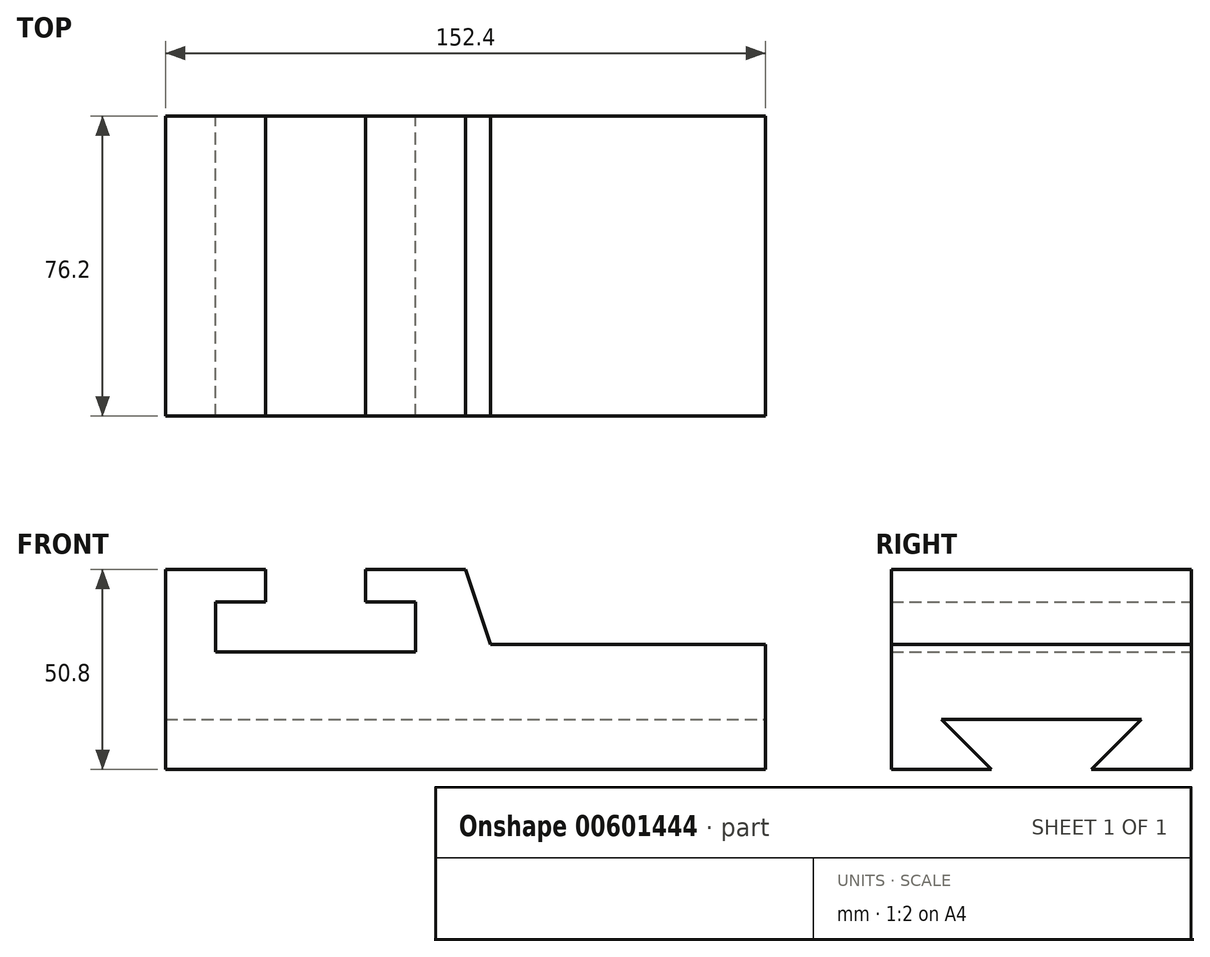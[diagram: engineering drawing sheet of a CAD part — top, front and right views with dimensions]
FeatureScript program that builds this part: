
annotation { "Feature Type Name" : "Feature", "Feature Type Description" : "" }
export const myFeature = defineFeature(function(context is Context, id is Id, definition is map)
    precondition{}
    {
        {
            var Q0;
            Q0=qCreatedBy(makeId("Front.planeOp"),FACE);
            var sketch = newSketch(context, id + "F0", { "sketchPlane" : qUnion([Q0])});
            skLineSegment(sketch, "E0", {"start": v(-82.55, 19.05) * mm, "end": v(-82.55, -31.75) * mm});
            skLineSegment(sketch, "E1", {"start": v(-82.55, -31.75) * mm, "end": v(69.85, -31.75) * mm});
            skLineSegment(sketch, "E2", {"start": v(69.85, -31.75) * mm, "end": v(69.85, 0) * mm});
            skLineSegment(sketch, "E3", {"start": v(69.85, 0) * mm, "end": v(0, 0) * mm});
            skLineSegment(sketch, "E4", {"start": v(0, 0) * mm, "end": v(-6.35, 19.05) * mm});
            skLineSegment(sketch, "E5", {"start": v(-6.35, 19.05) * mm, "end": v(-31.75, 19.05) * mm});
            skLineSegment(sketch, "E6", {"start": v(-31.75, 19.05) * mm, "end": v(-31.75, 10.85) * mm});
            skLineSegment(sketch, "E7", {"start": v(-31.75, 10.85) * mm, "end": v(-19.05, 10.85) * mm});
            skLineSegment(sketch, "E8", {"start": v(-19.05, 10.85) * mm, "end": v(-19.05, -1.85) * mm});
            skLineSegment(sketch, "E9", {"start": v(-19.05, -1.85) * mm, "end": v(-69.85, -1.85) * mm});
            skLineSegment(sketch, "E10", {"start": v(-69.85, -1.85) * mm, "end": v(-69.85, 10.85) * mm});
            skLineSegment(sketch, "E11", {"start": v(-69.85, 10.85) * mm, "end": v(-57.15, 10.85) * mm});
            skLineSegment(sketch, "E12", {"start": v(-57.15, 10.85) * mm, "end": v(-57.15, 19.05) * mm});
            skLineSegment(sketch, "E13", {"start": v(-57.15, 19.05) * mm, "end": v(-82.55, 19.05) * mm});
            skSolve(sketch);
        }
        {
            var Q0;
            Q0=makeQuery(id+"F0.imprint","IMPRINT",FACE,{"disambiguationData":[TD([[makeQuery(id+"F0.imprint","IMPRINT",EDGE,{"derivedFrom":sQuery(id+"F0.wireOp",EDGE,"E0")}),1.0]])]});
            extrude(context, id + "F1", {"entities" : qUnion([Q0]), "depth" : 76.2 * mm, "offsetDistance" : 25.4 * mm});
        }
        {
            var Q0;
            Q0=makeQuery(id+"F1.opExtrude","SWEPT_FACE",FACE,{"disambiguationData":[OSD([sQuery(id+"F0.wireOp",EDGE,"E2")])]});
            var sketch = newSketch(context, id + "F2", { "sketchPlane" : qUnion([Q0])});
            skLineSegment(sketch, "E14", {"start": v(-76.2, -31.75) * mm, "end": v(-50.8, -31.75) * mm});
            skLineSegment(sketch, "E15", {"start": v(0, -31.75) * mm, "end": v(-25.4, -31.75) * mm});
            skLineSegment(sketch, "E16", {"start": v(-25.4, -31.75) * mm, "end": v(-50.8, -31.75) * mm});
            skLineSegment(sketch, "E17", {"start": v(-50.8, -31.75) * mm, "end": v(-63.5, -19.05) * mm});
            skLineSegment(sketch, "E18", {"start": v(-25.4, -31.75) * mm, "end": v(-12.7, -19.05) * mm});
            skLineSegment(sketch, "E19", {"start": v(-12.7, -19.05) * mm, "end": v(-63.5, -19.05) * mm});
            skSolve(sketch);
        }
        {
            var Q0;
            Q0=makeQuery(id+"F2.imprint","IMPRINT",FACE,{"disambiguationData":[TD([[makeQuery(id+"F2.imprint","IMPRINT",EDGE,{"derivedFrom":sQuery(id+"F2.wireOp",EDGE,"E16")}),1.0]])]});
            extrude(context, id + "F3", {"entities" : qUnion([Q0]), "operationType" : NewBodyOperationType.REMOVE, "oppositeDirection" : true, "depth" : 152.4 * mm, "offsetDistance" : 25.4 * mm});
        }
    });
